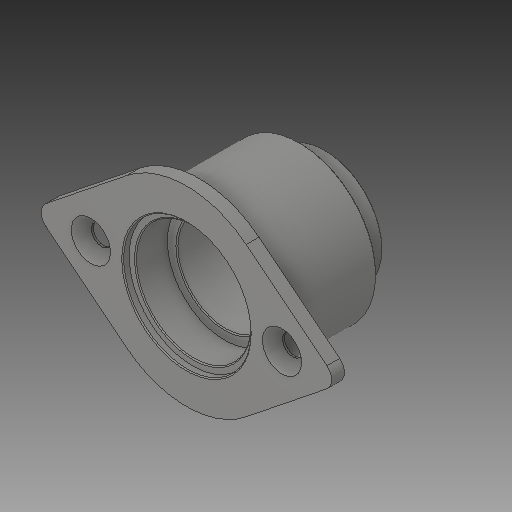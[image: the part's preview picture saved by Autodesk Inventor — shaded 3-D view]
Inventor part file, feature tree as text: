
AUTODESK INVENTOR PART (.ipt)
format: ipt  version: 2017 (Build 210142000, 142)  size: 177,664 bytes
history: native  units: in
note: dims shown in document units (in); Inventor stores cm internally (conversion verified against a paired STEP export)
features: chamfer x1
ambient origin geometry x8: Origin, YZ Plane, XZ Plane, XY Plane, X Axis, Y Axis, Z Axis, Center Point
bodies: Solid1 (feature_tree)
feature tree (1):
  chamfer  "Chamfer1"  [1 undecoded]
note: 1 required parameter value undecoded (feature->parameter linkage not recoverable at this tier; creation-order binding heuristic only, values carry confidence <= 0.55)
